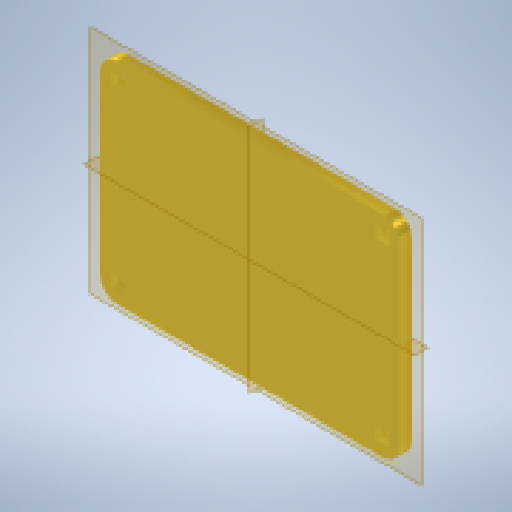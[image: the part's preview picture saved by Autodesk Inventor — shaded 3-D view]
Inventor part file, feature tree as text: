
AUTODESK INVENTOR PART (.ipt)
format: ipt  version: 2025.2 (Build 292293000, 293)  size: 167,936 bytes
history: native  units: mm
features: other x10, extrude x2, sketch x2, fillet x1
ambient origin geometry x8: Origin, YZ Plane, XZ Plane, XY Plane, X Axis, Y Axis, Z Axis, Center Point
bodies: Body1 (feature_tree)
feature tree (15):
  other  "Sólido1"
  extrude  "Extrusão1"  Depth=350.0mm
  fillet  "Arredondamento1"  Radius=20.0mm
  extrude  "Extrusão2"  Depth=20.0mm
  sketch  "Esboço1"  dims[d0=500.0mm d1=350.0mm d2=20.0mm d3=0.0mm]
  sketch  "Esboço2"  dims[d4=30.0mm d5=0.2mm d6=0.2mm d7=0.2mm d8=0.2mm d9=20.0mm d10=0.0mm d11=0.5mm d12=0.872665mm d13=0.5mm d14=0.872665mm]
  other  "Referência1"
  other  "Referência2"
  other  "Referência3"
  other  "Referência4"
  other  "Sessao8_07_04_2025_999_0001.iam"
  other  "Sessao8_07_04_2025_0002_0001:3"
  other  "Sessao8_07_04_2025_0002_0001:4"
  other  "Sessao8_07_04_2025_0002_0001:1"
  other  "Sessao8_07_04_2025_0002_0001:2"
